# Revit family: Spout-GROHE-Eurosmart_Cosmopolitan-13272000
name_source: partatom
category: Plumbing Fixtures
revit_build: Autodesk Revit 2014 (Build: 20130308_1515(x64)
units: mm (PartAtom-declared; Revit-internal decimal feet)

## types (1)
- 13272000
    Assembly Code = D2020300
    Cold Water Connection Diameter = 1/2"
    Cold Water Connection Radius = 1/4"
    Default Elevation = 21"
    Description = Tub spout
    Finish = Metal-Grohe-000-Chrome
    Flow Rate = 1.5 gpm (5.7 L/min)
    Height = 3 1/8"
    Hot Water Connection Diameter = 1"
    Hot Water Connection Radius = 1/4"
    Installation Type = Wall Mounted
    Length = 6 11/16"
    Manufacturer = Grohe
    Material = Metal-Grohe-000-Chrome
    Model = 13272000
    Price = Prices may vary. Please consult Manufacturer Representative for most up-to-date price list.
    Product Page URL = https://www.grohe.us
    Shipping Weight = 2.304 lb
    Tempered Connection Diameter = 1/2"
    Tempered Connection Radius = 1/4"
    URL = https://www.grohe.us
    Warranty Documentation Link = https://cdn.cloud.grohe.com
    Width = 3 1/8"

## geometry (parser evidence)
native form markers: Sweep x3
no freeform markers — native parametric forms only
